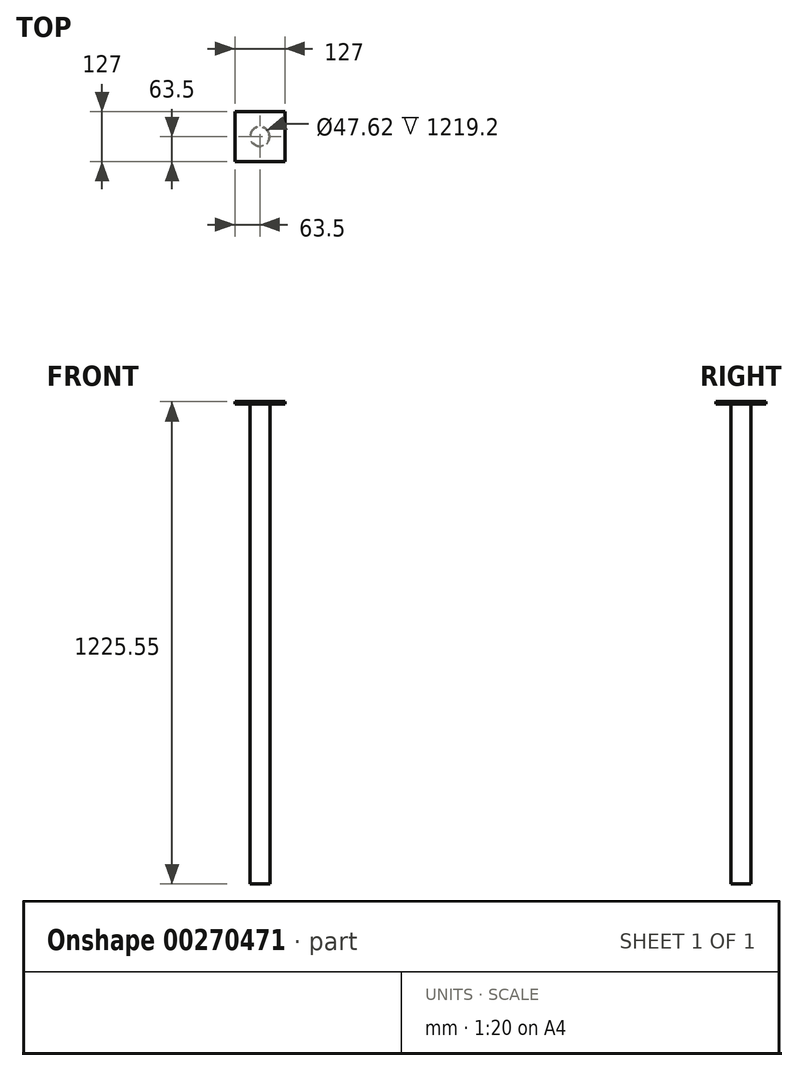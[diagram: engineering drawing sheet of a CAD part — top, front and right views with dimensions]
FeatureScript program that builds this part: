
annotation { "Feature Type Name" : "Feature", "Feature Type Description" : "" }
export const myFeature = defineFeature(function(context is Context, id is Id, definition is map)
    precondition{}
    {
        {
            var Q0;
            Q0=qCreatedBy(makeId("Top.planeOp"),FACE);
            var sketch = newSketch(context, id + "F0", { "sketchPlane" : qUnion([Q0])});
            skCircle(sketch, "E0", {"center": v(0, 0) * mm, "radius": 25.4 * mm});
            skCircle(sketch, "E1", {"center": v(0, 0) * mm, "radius": 23.81 * mm});
            skSolve(sketch);
        }
        {
            var Q0;
            Q0 = qSketchRegion(id + "F0", true);
            extrude(context, id + "F1", {"entities" : qUnion([Q0]), "depth" : 1219.2 * mm});
        }
        {
            var Q0;
            Q0=makeQuery(id+"F1.opExtrude","CAP_FACE",FACE,{"disambiguationData":[OSD([sQuery(id+"F0.wireOp",EDGE,"E0"),sQuery(id+"F0.wireOp",EDGE,"E1")])],"isStart":false});
            var sketch = newSketch(context, id + "F2", { "sketchPlane" : qUnion([Q0])});
            skLineSegment(sketch, "E2.bottom", {"start": v(63.5, 63.5) * mm, "end": v(-63.5, 63.5) * mm});
            skLineSegment(sketch, "E2.top", {"start": v(63.5, -63.5) * mm, "end": v(-63.5, -63.5) * mm});
            skLineSegment(sketch, "E2.left", {"start": v(63.5, 63.5) * mm, "end": v(63.5, -63.5) * mm});
            skLineSegment(sketch, "E2.right", {"start": v(-63.5, 63.5) * mm, "end": v(-63.5, -63.5) * mm});
            skPoint(sketch, "E2.middle", {"position": v(0, 0) * mm});
            skSolve(sketch);
        }
        {
            var Q0;
            Q0 = qSketchRegion(id + "F2", true);
            extrude(context, id + "F3", {"entities" : qUnion([Q0]), "operationType" : NewBodyOperationType.ADD, "depth" : 6.35 * mm});
        }
    });
